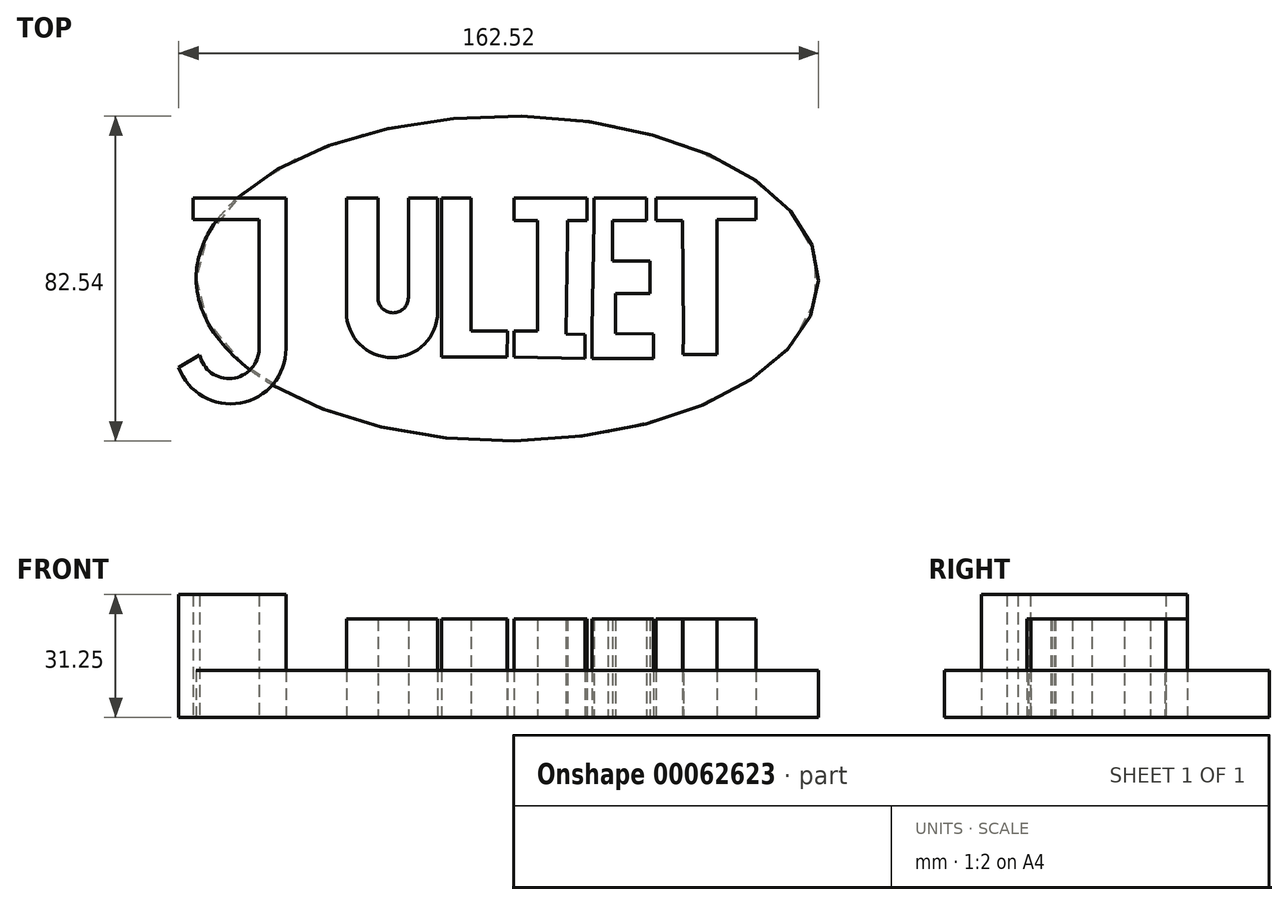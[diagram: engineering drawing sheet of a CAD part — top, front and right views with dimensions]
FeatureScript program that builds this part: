
annotation { "Feature Type Name" : "Feature", "Feature Type Description" : "" }
export const myFeature = defineFeature(function(context is Context, id is Id, definition is map)
    precondition{}
    {
        {
            var Q0;
            Q0=qCreatedBy(makeId("Top.planeOp"),FACE);
            var sketch = newSketch(context, id + "F0", { "sketchPlane" : qUnion([Q0])});
            skLineSegment(sketch, "E0", {"start": v(-40.25, 65.37) * mm, "end": v(-59.11, 65.37) * mm});
            skLineSegment(sketch, "E1", {"start": v(-12.27, 65.37) * mm, "end": v(-12.27, 30.32) * mm});
            skLineSegment(sketch, "E2", {"start": v(-59.11, 65.37) * mm, "end": v(-59.11, 60.94) * mm});
            skLineSegment(sketch, "E3", {"start": v(-59.11, 60.94) * mm, "end": v(-45.74, 60.94) * mm});
            skLineSegment(sketch, "E4", {"start": v(-20.75, 65.37) * mm, "end": v(-20.75, 40.04) * mm});
            skLineSegment(sketch, "E5", {"start": v(-31.7, 65.37) * mm, "end": v(-28.5, 65.37) * mm});
            skLineSegment(sketch, "E6", {"start": v(-28.5, 65.37) * mm, "end": v(-28.5, 40.04) * mm});
            skArc(sketch, "E7", {"start": v(-28.5, 40.04) * mm, "mid": v(-24.62, 36.16) * mm, "end": v(-20.75, 40.04) * mm});
            skLineSegment(sketch, "E8", {"start": v(-12.27, 65.37) * mm, "end": v(-4.77, 65.37) * mm});
            skLineSegment(sketch, "E9", {"start": v(-4.77, 65.37) * mm, "end": v(-4.77, 37.95) * mm});
            skLineSegment(sketch, "E10", {"start": v(-12.27, 30.32) * mm, "end": v(-12.27, 24.91) * mm});
            skLineSegment(sketch, "E11", {"start": v(-12.27, 24.91) * mm, "end": v(4.33, 24.91) * mm});
            skLineSegment(sketch, "E12", {"start": v(4.33, 24.91) * mm, "end": v(4.46, 32.04) * mm});
            skLineSegment(sketch, "E13", {"start": v(-4.77, 37.95) * mm, "end": v(-4.77, 31.55) * mm});
            skLineSegment(sketch, "E14", {"start": v(-4.77, 31.55) * mm, "end": v(4.46, 31.55) * mm});
            skPoint(sketch, "E15.start.orphan", {"position": v(0, 34.55) * mm});
            skLineSegment(sketch, "E16", {"start": v(24.19, 30.69) * mm, "end": v(19.3, 30.77) * mm});
            skLineSegment(sketch, "E17", {"start": v(-4.77, 61.26) * mm, "end": v(-4.77, 65.37) * mm});
            skLineSegment(sketch, "E18", {"start": v(12.5, 66.23) * mm, "end": v(12.5, 65.37) * mm});
            skLineSegment(sketch, "E19", {"start": v(19.3, 30.77) * mm, "end": v(19.72, 55.9) * mm});
            skPoint(sketch, "E20.endSnap0", {"position": v(3.87, 65.37) * mm});
            skLineSegment(sketch, "E21", {"start": v(24.67, 65.37) * mm, "end": v(12.5, 65.37) * mm});
            skLineSegment(sketch, "E22", {"start": v(12.12, 31.55) * mm, "end": v(12.12, 55.43) * mm});
            skLineSegment(sketch, "E23", {"start": v(12.12, 55.43) * mm, "end": v(12.12, 59.6) * mm});
            skLineSegment(sketch, "E24", {"start": v(19.72, 55.9) * mm, "end": v(19.72, 59.6) * mm});
            skLineSegment(sketch, "E25", {"start": v(26.45, 65.37) * mm, "end": v(26.45, 59.6) * mm});
            skLineSegment(sketch, "E26", {"start": v(26.45, 59.6) * mm, "end": v(25.97, 31.84) * mm});
            skLineSegment(sketch, "E27", {"start": v(25.97, 31.84) * mm, "end": v(25.97, 30.66) * mm});
            skPoint(sketch, "E28.trimOffspring.end.orphan", {"position": v(25.97, 25.2) * mm});
            skPoint(sketch, "E28.trimOffspring.start.orphan", {"position": v(25.97, 28.52) * mm});
            skLineSegment(sketch, "E29", {"start": v(25.97, 25.2) * mm, "end": v(25.97, 30.66) * mm});
            skLineSegment(sketch, "E30", {"start": v(26.45, 65.37) * mm, "end": v(29.96, 65.3) * mm});
            skLineSegment(sketch, "E31", {"start": v(29.96, 65.3) * mm, "end": v(39.73, 65.3) * mm});
            skLineSegment(sketch, "E32", {"start": v(39.73, 65.3) * mm, "end": v(39.73, 59.6) * mm});
            skLineSegment(sketch, "E33", {"start": v(39.73, 59.6) * mm, "end": v(31.14, 59.6) * mm});
            skLineSegment(sketch, "E34", {"start": v(31.14, 59.6) * mm, "end": v(31.14, 49.3) * mm});
            skLineSegment(sketch, "E35", {"start": v(31.14, 49.3) * mm, "end": v(40.65, 49.3) * mm});
            skLineSegment(sketch, "E36", {"start": v(40.65, 41.1) * mm, "end": v(31.92, 41.1) * mm});
            skLineSegment(sketch, "E37", {"start": v(31.92, 41.1) * mm, "end": v(31.92, 30.94) * mm});
            skLineSegment(sketch, "E38", {"start": v(42.14, 65.3) * mm, "end": v(67.61, 65.3) * mm});
            skLineSegment(sketch, "E39", {"start": v(67.61, 65.3) * mm, "end": v(67.61, 59.86) * mm});
            skLineSegment(sketch, "E40", {"start": v(67.61, 59.86) * mm, "end": v(57.71, 59.86) * mm});
            skLineSegment(sketch, "E41", {"start": v(57.71, 59.86) * mm, "end": v(57.71, 25.6) * mm});
            skLineSegment(sketch, "E42", {"start": v(57.71, 25.6) * mm, "end": v(48.98, 25.6) * mm});
            skLineSegment(sketch, "E43", {"start": v(31.92, 30.94) * mm, "end": v(41.55, 30.77) * mm});
            skLineSegment(sketch, "E44", {"start": v(49.17, 30.77) * mm, "end": v(48.98, 25.6) * mm});
            skLineSegment(sketch, "E45", {"start": v(40.65, 41.1) * mm, "end": v(40.65, 49.3) * mm});
            skPoint(sketch, "E46.end.orphan", {"position": v(39.73, 59.19) * mm});
            skLineSegment(sketch, "E47", {"start": v(42.14, 59.6) * mm, "end": v(48.86, 59.6) * mm});
            skLineSegment(sketch, "E48", {"start": v(48.86, 59.6) * mm, "end": v(49.17, 30.77) * mm});
            skLineSegment(sketch, "E49", {"start": v(48.98, 25.6) * mm, "end": v(49.17, 30.77) * mm});
            skLineSegment(sketch, "E50", {"start": v(39.73, 65.3) * mm, "end": v(39.73, 64.16) * mm});
            skLineSegment(sketch, "E51", {"start": v(42.14, 65.3) * mm, "end": v(42.14, 59.6) * mm});
            skLineSegment(sketch, "E52", {"start": v(41.55, 30.77) * mm, "end": v(41.55, 24.94) * mm});
            skLineSegment(sketch, "E53", {"start": v(25.97, 24.57) * mm, "end": v(41.55, 24.57) * mm});
            skLineSegment(sketch, "E54", {"start": v(41.55, 24.57) * mm, "end": v(41.55, 24.94) * mm});
            skLineSegment(sketch, "E55", {"start": v(24.67, 65.37) * mm, "end": v(24.67, 59.2) * mm});
            skPoint(sketch, "E56.orphan", {"position": v(25.97, 23.12) * mm});
            skLineSegment(sketch, "E57", {"start": v(19.72, 59.6) * mm, "end": v(24.67, 59.6) * mm});
            skLineSegment(sketch, "E58", {"start": v(6.12, 65.37) * mm, "end": v(6.12, 59.6) * mm});
            skLineSegment(sketch, "E59", {"start": v(6.12, 31.55) * mm, "end": v(6.12, 24.88) * mm});
            skLineSegment(sketch, "E60", {"start": v(6.12, 65.37) * mm, "end": v(12.5, 65.37) * mm});
            skLineSegment(sketch, "E61", {"start": v(6.12, 59.6) * mm, "end": v(12.12, 59.6) * mm});
            skLineSegment(sketch, "E62", {"start": v(24.19, 30.69) * mm, "end": v(24.08, 24.57) * mm});
            skLineSegment(sketch, "E63", {"start": v(6.46, 31.55) * mm, "end": v(12.12, 31.55) * mm});
            skLineSegment(sketch, "E64", {"start": v(6.46, 31.55) * mm, "end": v(6.12, 31.55) * mm});
            skLineSegment(sketch, "E65", {"start": v(6.12, 31.55) * mm, "end": v(6.46, 31.55) * mm});
            skLineSegment(sketch, "E66", {"start": v(6.12, 24.88) * mm, "end": v(24.08, 24.57) * mm});
            skLineSegment(sketch, "E67", {"start": v(-20.75, 65.37) * mm, "end": v(-13.3, 65.37) * mm});
            skLineSegment(sketch, "E68", {"start": v(-31.7, 65.37) * mm, "end": v(-36.5, 65.37) * mm});
            skLineSegment(sketch, "E69", {"start": v(25.97, 24.57) * mm, "end": v(25.97, 25.2) * mm});
            skPoint(sketch, "E70.end.orphan", {"position": v(-36.5, 25.05) * mm});
            skPoint(sketch, "E71.end.orphan", {"position": v(-13.3, 25.05) * mm});
            skPoint(sketch, "E72.end.orphan", {"position": v(-36.5, 31.2) * mm});
            skPoint(sketch, "E73.end.orphan", {"position": v(-13.3, 31.2) * mm});
            skPoint(sketch, "E74.start.orphan", {"position": v(-36.5, 64.68) * mm});
            skLineSegment(sketch, "E75", {"start": v(-36.5, 65.37) * mm, "end": v(-36.5, 36.38) * mm});
            skLineSegment(sketch, "E76", {"start": v(-36.5, 36.38) * mm, "end": v(-36.5, 65.37) * mm});
            skLineSegment(sketch, "E77", {"start": v(-13.3, 65.37) * mm, "end": v(-13.3, 36.38) * mm});
            skPoint(sketch, "E78.end.orphan", {"position": v(-13.3, 32.24) * mm});
            skPoint(sketch, "E78.start.orphan", {"position": v(-36.5, 32.24) * mm});
            skArc(sketch, "E79", {"start": v(-36.5, 36.38) * mm, "mid": v(-24.9, 24.79) * mm, "end": v(-13.3, 36.38) * mm});
            skPoint(sketch, "E80.start.orphan", {"position": v(-59.85, 33.47) * mm});
            skPoint(sketch, "E81.end.orphan", {"position": v(-54.44, 33.47) * mm});
            skPoint(sketch, "E82.end.orphan", {"position": v(-41.08, 33.47) * mm});
            skLineSegment(sketch, "E83", {"start": v(-45.74, 60.94) * mm, "end": v(-45.74, 40.11) * mm});
            skLineSegment(sketch, "E84", {"start": v(-40.25, 65.37) * mm, "end": v(-40.25, 38.94) * mm});
            skLineSegment(sketch, "E85", {"start": v(-45.74, 40.11) * mm, "end": v(-45.74, 37) * mm});
            skLineSegment(sketch, "E86", {"start": v(-45.74, 37) * mm, "end": v(-45.74, 40.11) * mm});
            skLineSegment(sketch, "E87", {"start": v(-40.25, 38.94) * mm, "end": v(-40.25, 37) * mm});
            skLineSegment(sketch, "E88", {"start": v(-45.74, 37) * mm, "end": v(-45.74, 34.73) * mm});
            skLineSegment(sketch, "E89", {"start": v(-45.74, 34.73) * mm, "end": v(-45.74, 37) * mm});
            skLineSegment(sketch, "E90", {"start": v(-40.25, 37) * mm, "end": v(-40.25, 34.73) * mm});
            skArc(sketch, "E91", {"start": v(-45.74, 34.73) * mm, "mid": v(-51.2, 28.67) * mm, "end": v(-57.8, 33.47) * mm});
            skArc(sketch, "E92", {"start": v(-40.25, 34.73) * mm, "mid": v(-49.52, 23.67) * mm, "end": v(-62.03, 30.86) * mm});
            skLineSegment(sketch, "E93", {"start": v(-62.03, 30.86) * mm, "end": v(-57.8, 33.47) * mm});
            skSolve(sketch);
        }
        {
            var Q0;
            Q0=makeQuery(id+"F0.imprint","IMPRINT",FACE,{"disambiguationData":[TD([[makeQuery(id+"F0.imprint","IMPRINT",EDGE,{"derivedFrom":sQuery(id+"F0.wireOp",EDGE,"E4")}),1.0]])]});
            var Q1;
            Q1=makeQuery(id+"F0.imprint","IMPRINT",FACE,{"disambiguationData":[TD([[makeQuery(id+"F0.imprint","IMPRINT",EDGE,{"derivedFrom":sQuery(id+"F0.wireOp",EDGE,"E1")}),1.0]])]});
            var Q2;
            Q2=makeQuery(id+"F0.imprint","IMPRINT",FACE,{"disambiguationData":[TD([[makeQuery(id+"F0.imprint","IMPRINT",EDGE,{"derivedFrom":sQuery(id+"F0.wireOp",EDGE,"E38")}),-1.0]])]});
            var Q3;
            Q3=makeQuery(id+"F0.imprint","IMPRINT",FACE,{"disambiguationData":[TD([[makeQuery(id+"F0.imprint","IMPRINT",EDGE,{"derivedFrom":sQuery(id+"F0.wireOp",EDGE,"E25")}),1.0]])]});
            var Q4;
            Q4=makeQuery(id+"F0.imprint","IMPRINT",FACE,{"disambiguationData":[TD([[makeQuery(id+"F0.imprint","IMPRINT",EDGE,{"derivedFrom":sQuery(id+"F0.wireOp",EDGE,"E16")}),1.0]])]});
            var Q5;
            Q5=makeQuery(id+"F0.imprint","IMPRINT",FACE,{"disambiguationData":[TD([[makeQuery(id+"F0.imprint","IMPRINT",EDGE,{"derivedFrom":sQuery(id+"F0.wireOp",EDGE,"E0")}),1.0]])]});
            extrude(context, id + "F1", {"entities" : qUnion([Q0, Q1, Q2, Q3, Q4, Q5]), "depth" : 25 * mm});
        }
        {
            var Q0;
            Q0=qCreatedBy(makeId("Top.planeOp"),FACE);
            var sketch = newSketch(context, id + "F2", { "sketchPlane" : qUnion([Q0])});
            skPoint(sketch, "E94.center.orphan", {"position": v(0, 44.88) * mm});
            skEllipse(sketch, "E95", {"center": v(4.4, 44.88) * mm, "majorRadius": 79.06 * mm, "minorRadius": 41.27 * mm, "majorAxis": v(-1, 0)});
            skSolve(sketch);
        }
        {
            var Q0;
            Q0=makeQuery(id+"F2.imprint","IMPRINT",FACE,{"disambiguationData":[TD([[makeQuery(id+"F2.imprint","IMPRINT",EDGE,{"derivedFrom":sQuery(id+"F2.wireOp",EDGE,"E95")}),1.0]])]});
            extrude(context, id + "F3", {"entities" : qUnion([Q0]), "depth" : 12 * mm});
        }
        {
            var Q0;
            Q0=makeQuery(id+"F1.opExtrude","SWEPT_BODY",BODY,{"disambiguationData":[OSD([sQuery(id+"F0.wireOp",EDGE,"E0"),sQuery(id+"F0.wireOp",EDGE,"E2"),sQuery(id+"F0.wireOp",EDGE,"E3"),sQuery(id+"F0.wireOp",EDGE,"E83"),sQuery(id+"F0.wireOp",EDGE,"E84"),sQuery(id+"F0.wireOp",EDGE,"E86"),sQuery(id+"F0.wireOp",EDGE,"E87"),sQuery(id+"F0.wireOp",EDGE,"E89"),sQuery(id+"F0.wireOp",EDGE,"E90"),sQuery(id+"F0.wireOp",EDGE,"E91"),sQuery(id+"F0.wireOp",EDGE,"E92"),sQuery(id+"F0.wireOp",EDGE,"E93")])]});
            var Q1;
            Q1=sQuery(id+"F0.wireOp",VERTEX,"E60.start");
            transform(context, id + "F4", {"entities" : qUnion([Q0]), "transformType" : TransformType.SCALE_UNIFORMLY, "scale" : 1.25, "scalePoint" : qUnion([Q1]), "makeCopy" : false});
        }
        {
            var Q0;
            Q0=qCreatedBy(makeId("Top.planeOp"),FACE);
            var sketch = newSketch(context, id + "F5", { "sketchPlane" : qUnion([Q0])});
            skEllipse(sketch, "E96.0", {"center": v(3.97, 39.76) * mm, "majorRadius": 98.82 * mm, "minorRadius": 51.58 * mm, "majorAxis": v(-1, 0)});
            skLineSegment(sketch, "E97", {"start": v(-94.85, 39.76) * mm, "end": v(3.97, 39.76) * mm});
            skLineSegment(sketch, "E98", {"start": v(3.97, 75.79) * mm, "end": v(3.97, 39.76) * mm});
            skPoint(sketch, "E99", {"position": v(3.97, 75.79) * mm});
            skPoint(sketch, "E100", {"position": v(-36.03, 75.79) * mm});
            skPoint(sketch, "E101", {"position": v(43.97, 75.79) * mm});
            skSolve(sketch);
        }
        {
            var Q0;
            Q0=sQuery(id+"F5.wireOp",VERTEX,"E100");
            var Q1;
            Q1=sQuery(id+"F5.wireOp",VERTEX,"E99");
            var Q2;
            Q2=sQuery(id+"F5.wireOp",VERTEX,"E101");
            var Q3;
            Q3=makeQuery(id+"F1.opExtrude","SWEPT_BODY",BODY,{"disambiguationData":[OSD([sQuery(id+"F0.wireOp",EDGE,"E0"),sQuery(id+"F0.wireOp",EDGE,"E2"),sQuery(id+"F0.wireOp",EDGE,"E3"),sQuery(id+"F0.wireOp",EDGE,"E83"),sQuery(id+"F0.wireOp",EDGE,"E84"),sQuery(id+"F0.wireOp",EDGE,"E86"),sQuery(id+"F0.wireOp",EDGE,"E87"),sQuery(id+"F0.wireOp",EDGE,"E89"),sQuery(id+"F0.wireOp",EDGE,"E90"),sQuery(id+"F0.wireOp",EDGE,"E91"),sQuery(id+"F0.wireOp",EDGE,"E92"),sQuery(id+"F0.wireOp",EDGE,"E93")])]});
            hole(context, id + "F6", {"style" : HoleStyle.SIMPLE, "holeDiameter" : 5 * mm, "endStyle" : HoleEndStyle.THROUGH, "oppositeDirection" : true, "locations" : qUnion([Q0, Q1, Q2]), "scope" : qUnion([Q3])});
        }
    });
